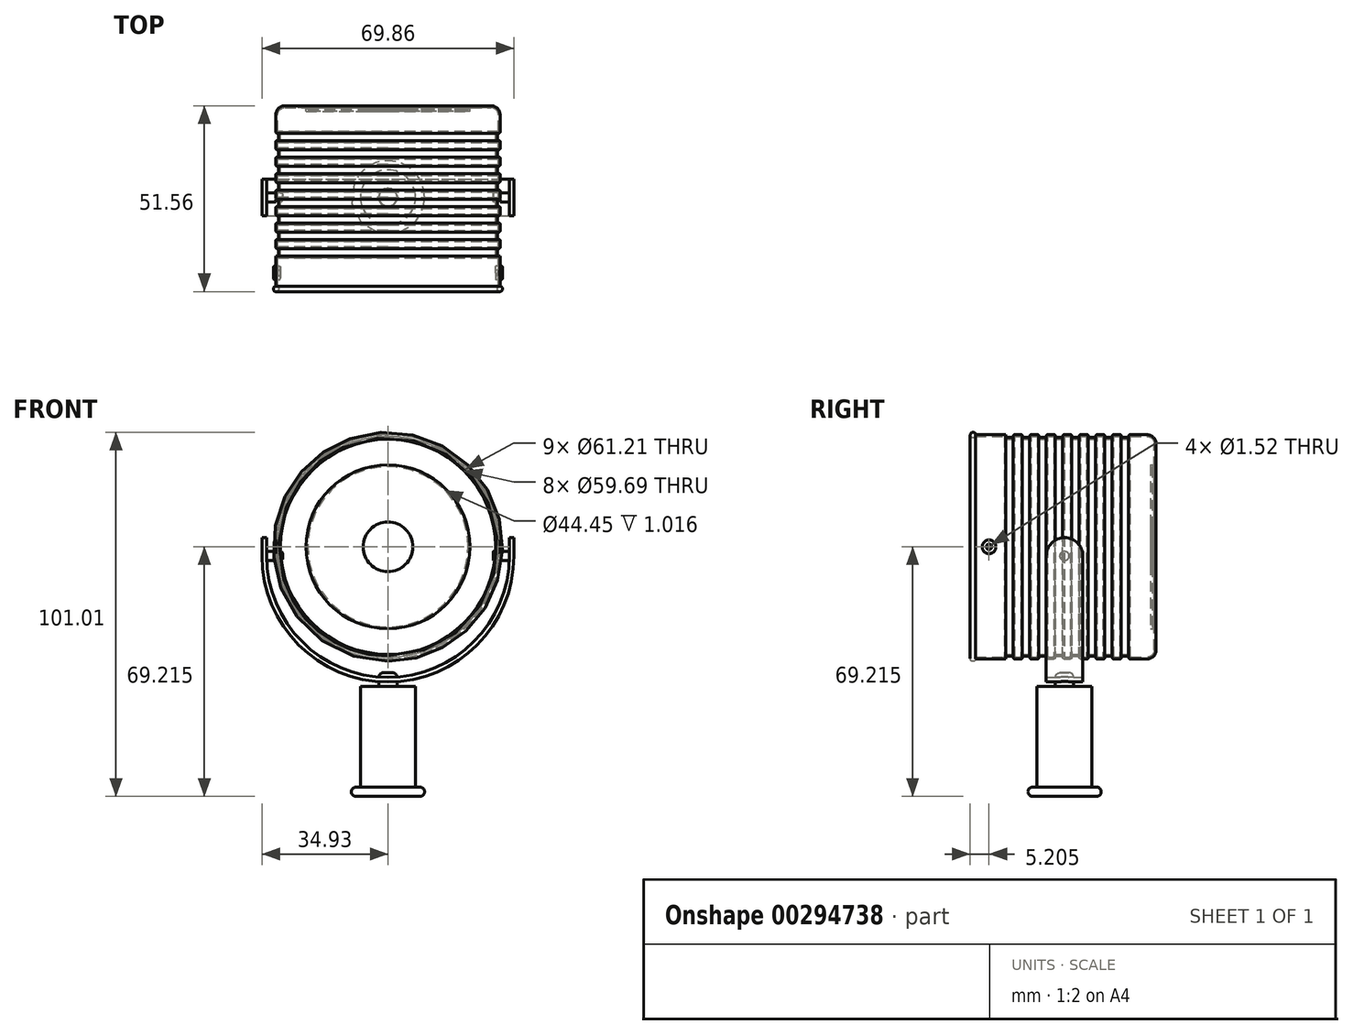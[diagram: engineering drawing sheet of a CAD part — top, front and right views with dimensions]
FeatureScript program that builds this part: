
annotation { "Feature Type Name" : "Feature", "Feature Type Description" : "" }
export const myFeature = defineFeature(function(context is Context, id is Id, definition is map)
    precondition{}
    {
        {
            var Q0;
            Q0=qCreatedBy(makeId("Top.planeOp"),FACE);
            var sketch = newSketch(context, id + "F0", { "sketchPlane" : qUnion([Q0])});
            skCircle(sketch, "E0", {"center": v(0, 0) * mm, "radius": 7.62 * mm});
            skSolve(sketch);
        }
        {
            var Q0;
            Q0=qSketchRegion(id+"F0",true);
            extrude(context, id + "F1", {"entities" : qUnion([Q0]), "depth" : 30.48 * mm});
        }
        {
            var Q0;
            Q0=qCreatedBy(makeId("Top.planeOp"),FACE);
            var sketch = newSketch(context, id + "F2", { "sketchPlane" : qUnion([Q0])});
            skCircle(sketch, "E1", {"center": v(0, 0) * mm, "radius": 10.16 * mm});
            skSolve(sketch);
        }
        {
            var Q0;
            Q0=qSketchRegion(id+"F2",true);
            extrude(context, id + "F3", {"entities" : qUnion([Q0]), "operationType" : NewBodyOperationType.ADD, "depth" : 2.54 * mm});
        }
        {
            var Q0;
            Q0=makeQuery(id+"F3.opExtrude","CAP_EDGE",EDGE,{"disambiguationData":[OSD([sQuery(id+"F2.wireOp",EDGE,"E1")])],"isStart":false});
            var Q1;
            Q1=makeQuery(id+"F3.opExtrude","CAP_EDGE",EDGE,{"disambiguationData":[OSD([sQuery(id+"F2.wireOp",EDGE,"E1")])],"isStart":true});
            fillet(context, id + "F4", {"entities" : qUnion([Q0, Q1]), "radius" : 1.27 * mm, "tangentPropagation" : true, "allowEdgeOverflow" : false});
        }
        {
            var Q0;
            Q0=makeQuery(id+"F1.opExtrude","CAP_FACE",FACE,{"disambiguationData":[OSD([sQuery(id+"F0.wireOp",EDGE,"E0")])],"isStart":false});
            var sketch = newSketch(context, id + "F5", { "sketchPlane" : qUnion([Q0])});
            skCircle(sketch, "E2", {"center": v(0, 0) * mm, "radius": 2.54 * mm});
            skSolve(sketch);
        }
        {
            var Q0;
            Q0=qSketchRegion(id+"F5",true);
            extrude(context, id + "F6", {"entities" : qUnion([Q0]), "operationType" : NewBodyOperationType.ADD, "depth" : 3.8 * mm});
        }
        {
            var Q0;
            Q0=makeQuery(id+"F6.opExtrude","CAP_EDGE",EDGE,{"disambiguationData":[OSD([sQuery(id+"F5.wireOp",EDGE,"E2")])],"isStart":false});
            fillet(context, id + "F7", {"entities" : qUnion([Q0]), "radius" : 1.27 * mm, "tangentPropagation" : true, "allowEdgeOverflow" : false});
        }
        {
            var Q0;
            Q0=qCreatedBy(makeId("Front.planeOp"),FACE);
            var sketch = newSketch(context, id + "F8", { "sketchPlane" : qUnion([Q0])});
            skArc(sketch, "E3", {"start": v(-34.93, 66.67) * mm, "mid": v(0, 31.75) * mm, "end": v(34.93, 66.68) * mm});
            skArc(sketch, "E4", {"start": v(-33.66, 66.68) * mm, "mid": v(0, 33.02) * mm, "end": v(33.66, 66.68) * mm});
            skLineSegment(sketch, "E5", {"start": v(-34.93, 66.68) * mm, "end": v(-33.66, 66.68) * mm});
            skLineSegment(sketch, "E6.trimOffspring", {"start": v(33.66, 66.68) * mm, "end": v(34.93, 66.68) * mm});
            skSolve(sketch);
        }
        {
            var Q0;
            Q0=qSketchRegion(id+"F8",true);
            extrude(context, id + "F9", {"entities" : qUnion([Q0]), "operationType" : NewBodyOperationType.ADD, "endBound" : BoundingType.SYMMETRIC, "depth" : 10.16 * mm});
        }
        {
            var Q0;
            Q0=qCreatedBy(makeId("Right.planeOp"),FACE);
            var sketch = newSketch(context, id + "F10", { "sketchPlane" : qUnion([Q0])});
            skArc(sketch, "E7", {"start": v(5.08, 66.68) * mm, "mid": v(0, 71.76) * mm, "end": v(-5.08, 66.68) * mm});
            skLineSegment(sketch, "E8", {"start": v(-5.08, 66.68) * mm, "end": v(5.08, 66.68) * mm});
            skSolve(sketch);
        }
        {
            var Q0;
            Q0=qSketchRegion(id+"F10",true);
            extrude(context, id + "F11", {"entities" : qUnion([Q0]), "operationType" : NewBodyOperationType.ADD, "endBound" : BoundingType.SYMMETRIC, "depth" : 69.85 * mm});
        }
        {
            var Q0;
            Q0=qSketchRegion(id+"F10",true);
            extrude(context, id + "F12", {"entities" : qUnion([Q0]), "operationType" : NewBodyOperationType.REMOVE, "endBound" : BoundingType.SYMMETRIC, "oppositeDirection" : true, "depth" : 67.3 * mm});
        }
        {
            var Q0;
            Q0=qCreatedBy(makeId("Right.planeOp"),FACE);
            var sketch = newSketch(context, id + "F13", { "sketchPlane" : qUnion([Q0])});
            skCircle(sketch, "E9", {"center": v(0, 66.68) * mm, "radius": 1.27 * mm});
            skSolve(sketch);
        }
        {
            var Q0;
            Q0=qSketchRegion(id+"F13",true);
            extrude(context, id + "F14", {"entities" : qUnion([Q0]), "operationType" : NewBodyOperationType.ADD, "endBound" : BoundingType.SYMMETRIC, "depth" : 67.3 * mm});
        }
        {
            var Q0;
            Q0=qSketchRegion(id+"F13",true);
            extrude(context, id + "F15", {"entities" : qUnion([Q0]), "operationType" : NewBodyOperationType.REMOVE, "endBound" : BoundingType.SYMMETRIC, "oppositeDirection" : true, "depth" : 58.42 * mm});
        }
        {
            var Q0;
            Q0=qCreatedBy(makeId("Front.planeOp"),FACE);
            var sketch = newSketch(context, id + "F16", { "sketchPlane" : qUnion([Q0])});
            skCircle(sketch, "E10", {"center": v(0, 66.68) * mm, "radius": 31.12 * mm});
            skSolve(sketch);
        }
        {
            var Q0;
            Q0=qSketchRegion(id+"F16",true);
            extrude(context, id + "F17", {"entities" : qUnion([Q0]), "endBound" : BoundingType.SYMMETRIC, "depth" : 50.8 * mm});
        }
        {
            var Q0;
            Q0=makeQuery(id+"F17.opExtrude","CAP_EDGE",EDGE,{"disambiguationData":[OSD([sQuery(id+"F16.wireOp",EDGE,"E10")])],"isStart":true});
            fillet(context, id + "F18", {"entities" : qUnion([Q0]), "radius" : 2.54 * mm, "tangentPropagation" : true, "allowEdgeOverflow" : false});
        }
        {
            var Q0;
            Q0=makeQuery(id+"F17.opExtrude","CAP_FACE",FACE,{"disambiguationData":[OSD([sQuery(id+"F16.wireOp",EDGE,"E10")])],"isStart":true});
            var sketch = newSketch(context, id + "F19", { "sketchPlane" : qUnion([Q0])});
            skCircle(sketch, "E11", {"center": v(0, 66.68) * mm, "radius": 22.23 * mm});
            skCircle(sketch, "E12", {"center": v(0, 66.68) * mm, "radius": 6.99 * mm});
            skSolve(sketch);
        }
        {
            var Q0;
            Q0=qSketchRegion(id+"F19",true);
            extrude(context, id + "F20", {"entities" : qUnion([Q0]), "operationType" : NewBodyOperationType.REMOVE, "oppositeDirection" : true, "depth" : 1.02 * mm});
        }
        {
            var Q0;
            Q0=makeQuery(id+"F20.boolean.opBoolean","COPY",EDGE,{"derivedFrom":makeQuery(id+"F20.opExtrude","CAP_EDGE",EDGE,{"disambiguationData":[OSD([sQuery(id+"F19.wireOp",EDGE,"E11")])],"isStart":true})});
            var Q1;
            Q1=makeQuery(id+"F20.boolean.opBoolean","COPY",EDGE,{"derivedFrom":makeQuery(id+"F20.opExtrude","CAP_EDGE",EDGE,{"disambiguationData":[OSD([sQuery(id+"F19.wireOp",EDGE,"E12")])],"isStart":true})});
            fillet(context, id + "F21", {"entities" : qUnion([Q0, Q1]), "radius" : 12.7 * mm, "tangentPropagation" : true, "allowEdgeOverflow" : false});
        }
        {
            var Q0;
            Q0=qCreatedBy(makeId("Right.planeOp"),FACE);
            var sketch = newSketch(context, id + "F22", { "sketchPlane" : qUnion([Q0])});
            skLineSegment(sketch, "E13.2.0.0", {"start": v(-14.22, 97.8) * mm, "end": v(-14.22, 97.03) * mm});
            skLineSegment(sketch, "E13.2.0.1", {"start": v(-16.26, 97.03) * mm, "end": v(-14.22, 97.03) * mm});
            skLineSegment(sketch, "E13.2.0.2", {"start": v(-16.26, 97.8) * mm, "end": v(-14.22, 97.8) * mm});
            skLineSegment(sketch, "E13.2.0.3", {"start": v(-16.26, 97.8) * mm, "end": v(-16.26, 97.03) * mm});
            skLineSegment(sketch, "E13.3.0.0", {"start": v(-9.65, 97.8) * mm, "end": v(-9.65, 97.03) * mm});
            skLineSegment(sketch, "E13.3.0.1", {"start": v(-11.68, 97.03) * mm, "end": v(-9.65, 97.03) * mm});
            skLineSegment(sketch, "E13.3.0.2", {"start": v(-11.68, 97.8) * mm, "end": v(-9.65, 97.8) * mm});
            skLineSegment(sketch, "E13.3.0.3", {"start": v(-11.68, 97.8) * mm, "end": v(-11.68, 97.03) * mm});
            skLineSegment(sketch, "E13.4.0.0", {"start": v(-5.08, 97.8) * mm, "end": v(-5.08, 97.03) * mm});
            skLineSegment(sketch, "E13.4.0.1", {"start": v(-7.11, 97.03) * mm, "end": v(-5.08, 97.03) * mm});
            skLineSegment(sketch, "E13.4.0.2", {"start": v(-7.11, 97.8) * mm, "end": v(-5.08, 97.8) * mm});
            skLineSegment(sketch, "E13.4.0.3", {"start": v(-7.11, 97.8) * mm, "end": v(-7.11, 97.03) * mm});
            skLineSegment(sketch, "E13.5.0.0", {"start": v(-0.5, 97.8) * mm, "end": v(-0.5, 97.03) * mm});
            skLineSegment(sketch, "E13.5.0.1", {"start": v(-2.54, 97.03) * mm, "end": v(-0.5, 97.03) * mm});
            skLineSegment(sketch, "E13.5.0.2", {"start": v(-2.54, 97.8) * mm, "end": v(-0.5, 97.8) * mm});
            skLineSegment(sketch, "E13.5.0.3", {"start": v(-2.54, 97.8) * mm, "end": v(-2.54, 97.03) * mm});
            skLineSegment(sketch, "E13.6.0.0", {"start": v(4.06, 97.8) * mm, "end": v(4.06, 97.03) * mm});
            skLineSegment(sketch, "E13.6.0.1", {"start": v(2.03, 97.03) * mm, "end": v(4.06, 97.03) * mm});
            skLineSegment(sketch, "E13.6.0.2", {"start": v(2.03, 97.8) * mm, "end": v(4.06, 97.8) * mm});
            skLineSegment(sketch, "E13.6.0.3", {"start": v(2.03, 97.8) * mm, "end": v(2.03, 97.03) * mm});
            skLineSegment(sketch, "E13.7.0.0", {"start": v(8.64, 97.8) * mm, "end": v(8.64, 97.03) * mm});
            skLineSegment(sketch, "E13.7.0.1", {"start": v(6.6, 97.03) * mm, "end": v(8.64, 97.03) * mm});
            skLineSegment(sketch, "E13.7.0.2", {"start": v(6.6, 97.8) * mm, "end": v(8.64, 97.8) * mm});
            skLineSegment(sketch, "E13.7.0.3", {"start": v(6.6, 97.8) * mm, "end": v(6.6, 97.03) * mm});
            skLineSegment(sketch, "E13.8.0.0", {"start": v(13.2, 97.8) * mm, "end": v(13.2, 97.03) * mm});
            skLineSegment(sketch, "E13.8.0.1", {"start": v(11.18, 97.03) * mm, "end": v(13.2, 97.03) * mm});
            skLineSegment(sketch, "E13.8.0.2", {"start": v(11.18, 97.8) * mm, "end": v(13.2, 97.8) * mm});
            skLineSegment(sketch, "E13.8.0.3", {"start": v(11.18, 97.8) * mm, "end": v(11.18, 97.03) * mm});
            skLineSegment(sketch, "E13.9.0.0", {"start": v(17.78, 97.8) * mm, "end": v(17.78, 97.03) * mm});
            skLineSegment(sketch, "E13.9.0.1", {"start": v(15.75, 97.03) * mm, "end": v(17.78, 97.03) * mm});
            skLineSegment(sketch, "E13.9.0.2", {"start": v(15.75, 97.8) * mm, "end": v(17.78, 97.8) * mm});
            skLineSegment(sketch, "E13.9.0.3", {"start": v(15.75, 97.8) * mm, "end": v(15.75, 97.03) * mm});
            skSolve(sketch);
        }
        {
            var Q0;
            Q0=qSketchRegion(id+"F22",true);
            var Q1;
            Q1=makeQuery(id+"F17.opExtrude","SWEPT_FACE",FACE,{"disambiguationData":[OSD([sQuery(id+"F16.wireOp",EDGE,"E10")])]});
            revolve(context, id + "F23", {"operationType" : NewBodyOperationType.REMOVE, "entities" : qUnion([Q0]), "axis" : qUnion([Q1]), "revolveType" : RevolveType.FULL, "oppositeDirection" : true});
        }
        {
            var Q0;
            Q0=makeQuery(id+"F23.boolean.opBoolean","SPLIT",FACE,{"disambiguationData":[TD([makeQuery(id+"F23.opRevolve","SWEPT_FACE",FACE,{"disambiguationData":[OSD([sQuery(id+"F22.wireOp",EDGE,"E13.2.0.0")])]})])],"derivedFrom":makeQuery(id+"F17.opExtrude","SWEPT_FACE",FACE,{"disambiguationData":[OSD([sQuery(id+"F16.wireOp",EDGE,"E10")])]})});
            var Q1;
            Q1=makeQuery(id+"F23.boolean.opBoolean","COPY",EDGE,{"derivedFrom":makeQuery(id+"F23.opRevolve","SWEPT_EDGE",EDGE,{"disambiguationData":[OSD([sQuery(id+"F22.wireOp",EDGE,"E13.2.0.2"),sQuery(id+"F22.wireOp",EDGE,"E13.2.0.3")])]})});
            var Q2;
            Q2=makeQuery(id+"F23.boolean.opBoolean","SPLIT",FACE,{"disambiguationData":[TD([makeQuery(id+"F23.opRevolve","SWEPT_FACE",FACE,{"disambiguationData":[OSD([sQuery(id+"F22.wireOp",EDGE,"E13.3.0.0")])]})])],"derivedFrom":makeQuery(id+"F17.opExtrude","SWEPT_FACE",FACE,{"disambiguationData":[OSD([sQuery(id+"F16.wireOp",EDGE,"E10")])]})});
            var Q3;
            Q3=makeQuery(id+"F23.boolean.opBoolean","SPLIT",FACE,{"disambiguationData":[TD([makeQuery(id+"F23.opRevolve","SWEPT_FACE",FACE,{"disambiguationData":[OSD([sQuery(id+"F22.wireOp",EDGE,"E13.4.0.0")])]})])],"derivedFrom":makeQuery(id+"F17.opExtrude","SWEPT_FACE",FACE,{"disambiguationData":[OSD([sQuery(id+"F16.wireOp",EDGE,"E10")])]})});
            var Q4;
            Q4=makeQuery(id+"F23.boolean.opBoolean","SPLIT",FACE,{"disambiguationData":[TD([makeQuery(id+"F23.opRevolve","SWEPT_FACE",FACE,{"disambiguationData":[OSD([sQuery(id+"F22.wireOp",EDGE,"E13.5.0.0")])]})])],"derivedFrom":makeQuery(id+"F17.opExtrude","SWEPT_FACE",FACE,{"disambiguationData":[OSD([sQuery(id+"F16.wireOp",EDGE,"E10")])]})});
            var Q5;
            Q5=makeQuery(id+"F23.boolean.opBoolean","SPLIT",FACE,{"disambiguationData":[TD([makeQuery(id+"F23.opRevolve","SWEPT_FACE",FACE,{"disambiguationData":[OSD([sQuery(id+"F22.wireOp",EDGE,"E13.6.0.0")])]})])],"derivedFrom":makeQuery(id+"F17.opExtrude","SWEPT_FACE",FACE,{"disambiguationData":[OSD([sQuery(id+"F16.wireOp",EDGE,"E10")])]})});
            var Q6;
            Q6=makeQuery(id+"F23.boolean.opBoolean","SPLIT",FACE,{"disambiguationData":[TD([makeQuery(id+"F23.opRevolve","SWEPT_FACE",FACE,{"disambiguationData":[OSD([sQuery(id+"F22.wireOp",EDGE,"E13.7.0.0")])]})])],"derivedFrom":makeQuery(id+"F17.opExtrude","SWEPT_FACE",FACE,{"disambiguationData":[OSD([sQuery(id+"F16.wireOp",EDGE,"E10")])]})});
            var Q7;
            Q7=makeQuery(id+"F23.boolean.opBoolean","SPLIT",FACE,{"disambiguationData":[TD([makeQuery(id+"F23.opRevolve","SWEPT_FACE",FACE,{"disambiguationData":[OSD([sQuery(id+"F22.wireOp",EDGE,"E13.8.0.0")])]})])],"derivedFrom":makeQuery(id+"F17.opExtrude","SWEPT_FACE",FACE,{"disambiguationData":[OSD([sQuery(id+"F16.wireOp",EDGE,"E10")])]})});
            var Q8;
            Q8=makeQuery(id+"F23.boolean.opBoolean","COPY",EDGE,{"derivedFrom":makeQuery(id+"F23.opRevolve","SWEPT_EDGE",EDGE,{"disambiguationData":[OSD([sQuery(id+"F22.wireOp",EDGE,"E13.9.0.0"),sQuery(id+"F22.wireOp",EDGE,"E13.9.0.2")])]})});
            var Q9;
            Q9=makeQuery(id+"F23.boolean.opBoolean","COPY",FACE,{"derivedFrom":makeQuery(id+"F23.opRevolve","SWEPT_FACE",FACE,{"disambiguationData":[OSD([sQuery(id+"F22.wireOp",EDGE,"E13.2.0.1")])]})});
            var Q10;
            Q10=makeQuery(id+"F23.boolean.opBoolean","COPY",FACE,{"derivedFrom":makeQuery(id+"F23.opRevolve","SWEPT_FACE",FACE,{"disambiguationData":[OSD([sQuery(id+"F22.wireOp",EDGE,"E13.3.0.1")])]})});
            var Q11;
            Q11=makeQuery(id+"F23.boolean.opBoolean","COPY",FACE,{"derivedFrom":makeQuery(id+"F23.opRevolve","SWEPT_FACE",FACE,{"disambiguationData":[OSD([sQuery(id+"F22.wireOp",EDGE,"E13.4.0.1")])]})});
            var Q12;
            Q12=makeQuery(id+"F23.boolean.opBoolean","COPY",FACE,{"derivedFrom":makeQuery(id+"F23.opRevolve","SWEPT_FACE",FACE,{"disambiguationData":[OSD([sQuery(id+"F22.wireOp",EDGE,"E13.5.0.1")])]})});
            var Q13;
            Q13=makeQuery(id+"F23.boolean.opBoolean","COPY",FACE,{"derivedFrom":makeQuery(id+"F23.opRevolve","SWEPT_FACE",FACE,{"disambiguationData":[OSD([sQuery(id+"F22.wireOp",EDGE,"E13.6.0.1")])]})});
            var Q14;
            Q14=makeQuery(id+"F23.boolean.opBoolean","COPY",FACE,{"derivedFrom":makeQuery(id+"F23.opRevolve","SWEPT_FACE",FACE,{"disambiguationData":[OSD([sQuery(id+"F22.wireOp",EDGE,"E13.7.0.1")])]})});
            var Q15;
            Q15=makeQuery(id+"F23.boolean.opBoolean","COPY",FACE,{"derivedFrom":makeQuery(id+"F23.opRevolve","SWEPT_FACE",FACE,{"disambiguationData":[OSD([sQuery(id+"F22.wireOp",EDGE,"E13.8.0.1")])]})});
            var Q16;
            Q16=makeQuery(id+"F23.boolean.opBoolean","COPY",FACE,{"derivedFrom":makeQuery(id+"F23.opRevolve","SWEPT_FACE",FACE,{"disambiguationData":[OSD([sQuery(id+"F22.wireOp",EDGE,"E13.9.0.1")])]})});
            fillet(context, id + "F24", {"entities" : qUnion([Q0, Q1, Q2, Q3, Q4, Q5, Q6, Q7, Q8, Q9, Q10, Q11, Q12, Q13, Q14, Q15, Q16]), "radius" : 0.38 * mm, "tangentPropagation" : true, "allowEdgeOverflow" : false});
        }
        {
            var Q0;
            Q0=makeQuery(id+"F17.opExtrude","CAP_FACE",FACE,{"disambiguationData":[OSD([sQuery(id+"F16.wireOp",EDGE,"E10")])],"isStart":false});
            shell(context, id + "F25", {"entities" : qUnion([Q0]), "thickness" : 0.5 * mm});
        }
        {
            var Q0;
            Q0=makeQuery(id+"F15.boolean.opBoolean","COPY",EDGE,{"derivedFrom":makeQuery(id+"F15.opExtrude","CAP_EDGE",EDGE,{"disambiguationData":[OSD([sQuery(id+"F13.wireOp",EDGE,"E9")])],"isStart":false})});
            var Q1;
            Q1=makeQuery(id+"F15.boolean.opBoolean","COPY",EDGE,{"derivedFrom":makeQuery(id+"F15.opExtrude","CAP_EDGE",EDGE,{"disambiguationData":[OSD([sQuery(id+"F13.wireOp",EDGE,"E9")])],"isStart":true})});
            fillet(context, id + "F26", {"entities" : qUnion([Q0, Q1]), "radius" : 0.64 * mm, "tangentPropagation" : true, "allowEdgeOverflow" : false});
        }
        {
            var Q0;
            Q0=qCreatedBy(makeId("Right.planeOp"),FACE);
            var sketch = newSketch(context, id + "F27", { "sketchPlane" : qUnion([Q0])});
            skCircle(sketch, "E14", {"center": v(-20.96, 66.68) * mm, "radius": 1.9 * mm});
            skCircle(sketch, "E15", {"center": v(-20.96, 66.68) * mm, "radius": 0.76 * mm});
            skSolve(sketch);
        }
        {
            var Q0;
            Q0=qSketchRegion(id+"F27",true);
            extrude(context, id + "F28", {"entities" : qUnion([Q0]), "operationType" : NewBodyOperationType.ADD, "endBound" : BoundingType.SYMMETRIC, "depth" : 63.5 * mm});
        }
        {
            var Q0;
            Q0=qSketchRegion(id+"F27",true);
            extrude(context, id + "F29", {"entities" : qUnion([Q0]), "operationType" : NewBodyOperationType.REMOVE, "endBound" : BoundingType.SYMMETRIC, "oppositeDirection" : true, "depth" : 59.69 * mm});
        }
        {
            var Q0;
            Q0=makeQuery(id+"F28.opExtrude","CAP_EDGE",EDGE,{"disambiguationData":[OSD([sQuery(id+"F27.wireOp",EDGE,"E14")])],"isStart":false});
            var Q1;
            Q1=makeQuery(id+"F28.opExtrude","CAP_EDGE",EDGE,{"disambiguationData":[OSD([sQuery(id+"F27.wireOp",EDGE,"E15")])],"isStart":false});
            var Q2;
            Q2=makeQuery(id+"F29.boolean.opBoolean","COPY",EDGE,{"derivedFrom":makeQuery(id+"F29.opExtrude","CAP_EDGE",EDGE,{"disambiguationData":[OSD([sQuery(id+"F27.wireOp",EDGE,"E14")])],"isStart":true})});
            var Q3;
            Q3=makeQuery(id+"F29.boolean.opBoolean","COPY",EDGE,{"derivedFrom":makeQuery(id+"F29.opExtrude","CAP_EDGE",EDGE,{"disambiguationData":[OSD([sQuery(id+"F27.wireOp",EDGE,"E15")])],"isStart":true})});
            var Q4;
            Q4=makeQuery(id+"F28.opExtrude","CAP_EDGE",EDGE,{"disambiguationData":[OSD([sQuery(id+"F27.wireOp",EDGE,"E14")])],"isStart":true});
            var Q5;
            Q5=makeQuery(id+"F28.opExtrude","CAP_EDGE",EDGE,{"disambiguationData":[OSD([sQuery(id+"F27.wireOp",EDGE,"E15")])],"isStart":true});
            var Q6;
            Q6=makeQuery(id+"F29.boolean.opBoolean","COPY",EDGE,{"derivedFrom":makeQuery(id+"F29.opExtrude","CAP_EDGE",EDGE,{"disambiguationData":[OSD([sQuery(id+"F27.wireOp",EDGE,"E14")])],"isStart":false})});
            var Q7;
            Q7=makeQuery(id+"F29.boolean.opBoolean","COPY",EDGE,{"derivedFrom":makeQuery(id+"F29.opExtrude","CAP_EDGE",EDGE,{"disambiguationData":[OSD([sQuery(id+"F27.wireOp",EDGE,"E15")])],"isStart":false})});
            fillet(context, id + "F30", {"entities" : qUnion([Q0, Q1, Q2, Q3, Q4, Q5, Q6, Q7]), "radius" : 0.38 * mm, "tangentPropagation" : true, "allowEdgeOverflow" : false});
        }
        {
            var Q0;
            Q0=qCreatedBy(makeId("Front.planeOp"),FACE);
            cPlane(context, id + "F31", {"entities" : qUnion([Q0]), "cplaneType" : CPlaneType.OFFSET, "offset" : 24.13 * mm, "width" : 152.4 * mm, "height" : 152.4 * mm});
        }
        {
            var Q0;
            Q0=qCreatedBy(makeId("Right.planeOp"),FACE);
            var sketch = newSketch(context, id + "F32", { "sketchPlane" : qUnion([Q0])});
            skCircle(sketch, "E16", {"center": v(-25.4, 97.7) * mm, "radius": 0.76 * mm});
            skSolve(sketch);
        }
        {
            var Q0;
            Q0=qSketchRegion(id+"F32",true);
            var Q1;
            {var subQ0=sQuery(id+"F16.wireOp",EDGE,"E10");var subQ1=makeQuery(id+"F17.opExtrude","CAP_FACE",FACE,{"disambiguationData":[OSD([subQ0])],"isStart":false});var subQ2=sQuery(id+"F22.wireOp",EDGE,"E13.2.0.3");Q1=makeQuery(id+"F28.boolean.opBoolean","SPLIT",FACE,{"disambiguationData":[TD([subQ1,makeQuery(id+"F24.opFillet","BLEND_FACE",FACE,{"disambiguationData":[OSD([sQuery(id+"F22.wireOp",EDGE,"E13.2.0.2"),subQ2])]}),makeQuery(id+"F28.opExtrude","SWEPT_FACE",FACE,{"disambiguationData":[OSD([sQuery(id+"F27.wireOp",EDGE,"E14")])]})])],"derivedFrom":makeQuery(id+"F23.boolean.opBoolean","SPLIT",FACE,{"disambiguationData":[TD([subQ1])],"derivedFrom":makeQuery(id+"F17.opExtrude","SWEPT_FACE",FACE,{"disambiguationData":[OSD([subQ0])]})})});}
            revolve(context, id + "F33", {"operationType" : NewBodyOperationType.ADD, "entities" : qUnion([Q0]), "axis" : qUnion([Q1]), "revolveType" : RevolveType.FULL});
        }
        {
            var Q0;
            Q0=qCreatedBy(id+"F31.planeOp",FACE);
            var sketch = newSketch(context, id + "F34", { "sketchPlane" : qUnion([Q0])});
            skPoint(sketch, "E17", {"position": v(29.85, 66.68) * mm});
            skPoint(sketch, "E18", {"position": v(0, 66.68) * mm});
            skLineSegment(sketch, "E19", {"start": v(0, 0) * mm, "end": v(0, 2.54) * mm, "construction": true});
            skSolve(sketch);
        }
        {
            var Q0;
            Q0=makeQuery(id+"F1.opExtrude","SWEPT_BODY",BODY,{"disambiguationData":[OSD([sQuery(id+"F0.wireOp",EDGE,"E0")])]});
            var Q1;
            Q1=sQuery(id+"F34.wireOp",EDGE,"E19");
            transform(context, id + "F35", {"entities" : qUnion([Q0]), "transformType" : TransformType.TRANSLATION_ENTITY, "oppositeDirectionEntity" : true, "transformLine" : qUnion([Q1]), "makeCopy" : false});
        }
    });
